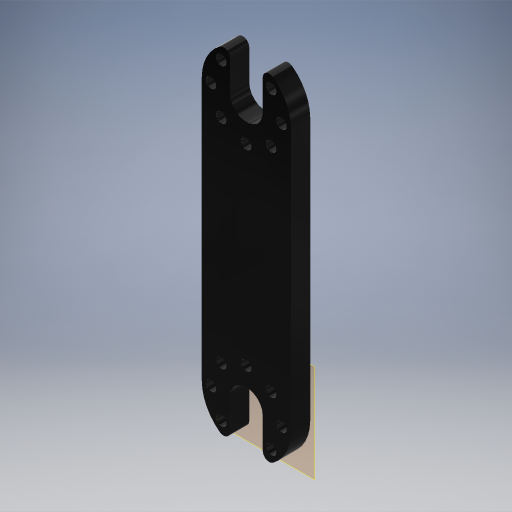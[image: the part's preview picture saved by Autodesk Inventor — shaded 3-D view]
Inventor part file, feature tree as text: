
AUTODESK INVENTOR PART (.ipt)
format: ipt  version: 2024 (Build 280153000, 153)  size: 318,464 bytes
history: native  units: in
note: dims shown in document units (in); Inventor stores cm internally (conversion verified against a paired STEP export)
features: other x4, extrude x1, mirror x1, fillet x1, sketch x1, reference x1
ambient origin geometry x8: Origin, YZ Plane, XZ Plane, XY Plane, X Axis, Y Axis, Z Axis, Center Point
bodies: Body1 (feature_tree)
feature tree (9):
  other  "솔리드4"
  other  "작업 평면1"
  extrude  "돌출4"  Depth=0.0039in
  mirror  "미러4"
  fillet  "모깎기3"  Radius=0.126in
  sketch  "스케치1"
  reference  "참조2"
  other  "조립품7"
  other  "64-106Horn:1"
